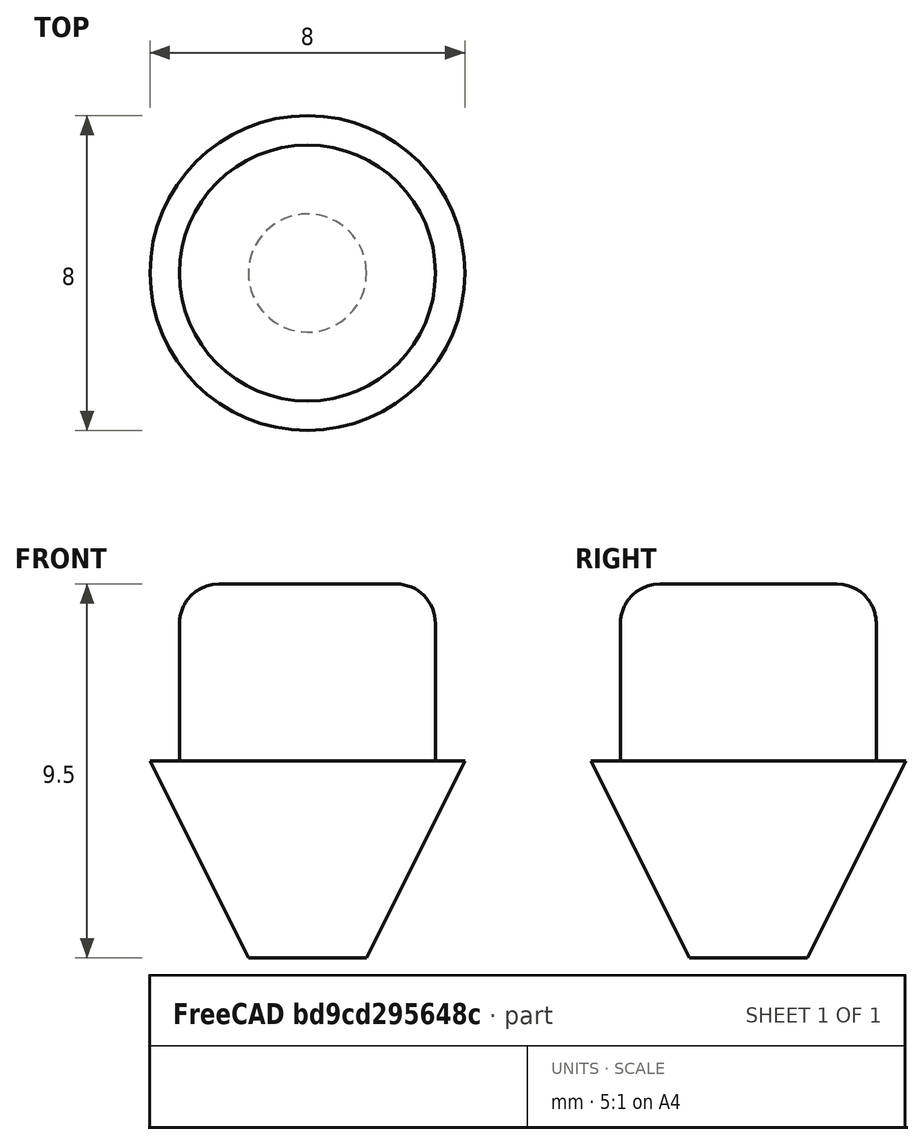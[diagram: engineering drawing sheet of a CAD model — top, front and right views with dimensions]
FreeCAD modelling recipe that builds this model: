
FCSTD DOCUMENT  (FreeCAD 1.0R39109 (Git))
Label: gbc_buttons_x_y_extenders
License: All rights reserved
LicenseURL: http://en.wikipedia.org/wiki/All_rights_reserved
objects: Mesh::Feature×1, Part::Cylinder×1, Part::Fillet×1, Part::Cone×1, Part::MultiFuse×1
note: 4 computed .brp shape members not serialized (recipe doc carries the construction recipe); baked Part::Feature solids carry a one-line shape summary decoded from their .brp

FEATURE [Mesh::Feature] gbc_retro_zero_x_y_clicky2
  Placement = pos=(0,20,0) rot=(0,0,1;0rad)
FEATURE [Part::Cylinder] Cylinder  label="Cylinder(button)"
  Angle = 360
  AttacherType = Attacher::AttachEngine3D
  FirstAngle = 0
  Height = 4.5
  Placement = pos=(0,0,0.5) rot=(0,0,1;0rad)
  Radius = 3.25
  SecondAngle = 0
FEATURE [Part::Fillet] Fillet
  Base = -> Cylinder
  EdgeLinks = -> Cylinder [Edge3]
  Edges = 1 edges r=1: [Edge3]
FEATURE [Part::Cone] Cone
  Angle = 360
  AttacherType = Attacher::AttachEngine3D
  Height = 5
  Placement = pos=(0,0,-4.5) rot=(0,0,1;0rad)
  Radius1 = 1.5
  Radius2 = 4
FEATURE [Part::MultiFuse] Fusion
  Shapes = -> [Fillet,Cone]
